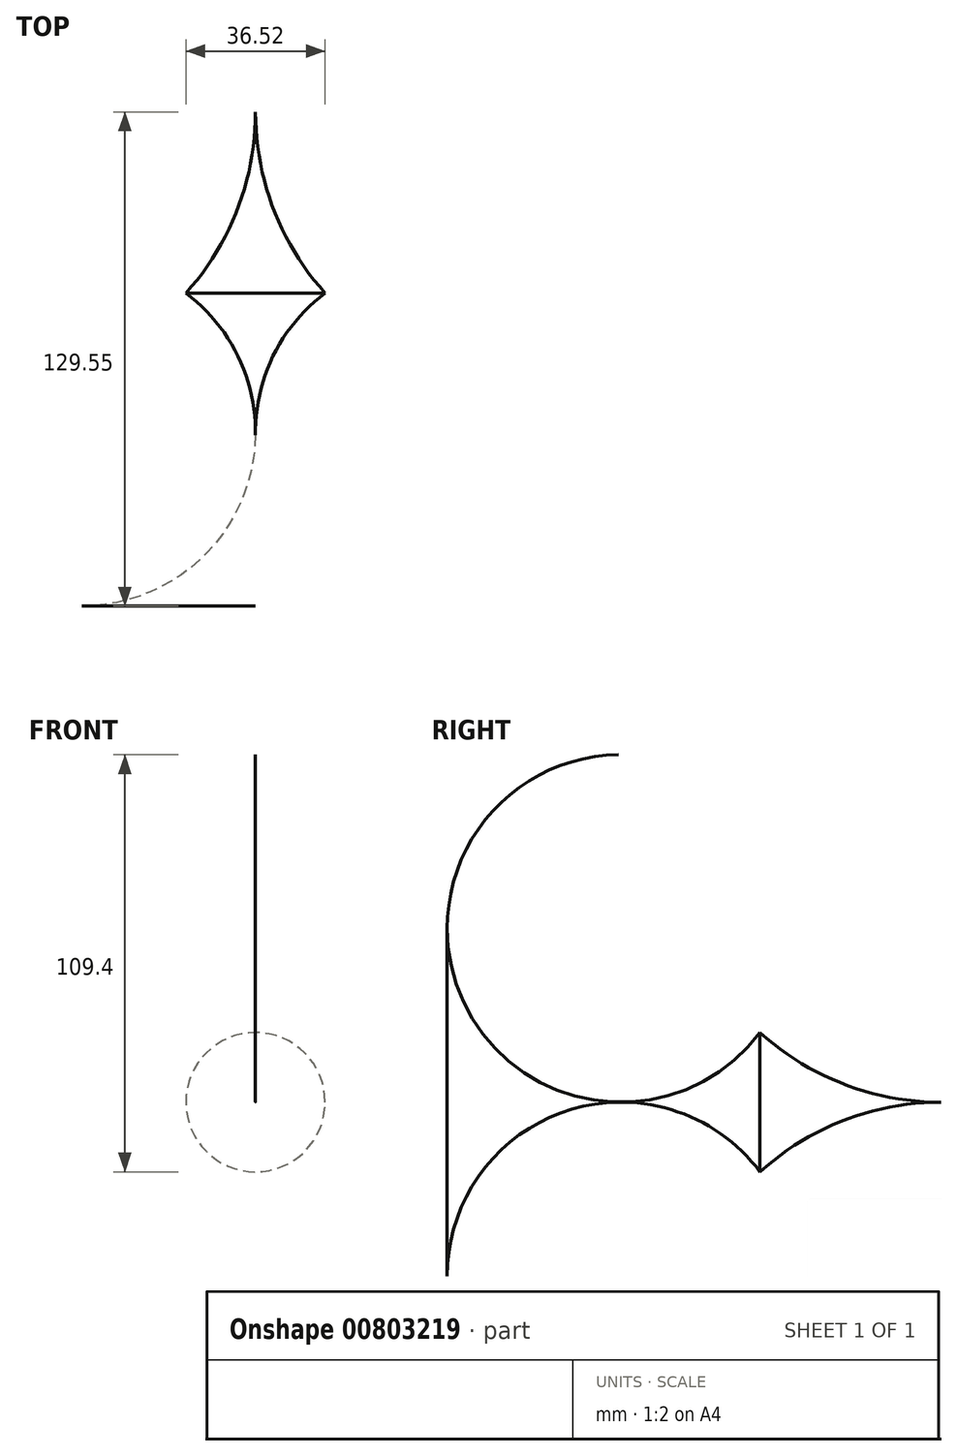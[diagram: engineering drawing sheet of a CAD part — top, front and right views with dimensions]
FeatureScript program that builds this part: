
annotation { "Feature Type Name" : "Feature", "Feature Type Description" : "" }
export const myFeature = defineFeature(function(context is Context, id is Id, definition is map)
    precondition{}
    {
        {
            var Q0;
            Q0=qCreatedBy(makeId("Top.planeOp"),FACE);
            var sketch = newSketch(context, id + "F0", { "sketchPlane" : qUnion([Q0])});
            skLineSegment(sketch, "E0", {"start": v(0, 75.28) * mm, "end": v(0, -76.95) * mm, "construction": true});
            skArc(sketch, "E1", {"start": v(18.26, 0) * mm, "mid": v(4.98, -15.77) * mm, "end": v(0, -35.79) * mm});
            skArc(sketch, "E2", {"start": v(0, 47.47) * mm, "mid": v(4.72, 22.04) * mm, "end": v(18.26, 0) * mm});
            skLineSegment(sketch, "E3", {"start": v(0, 47.47) * mm, "end": v(0, -35.79) * mm});
            skSolve(sketch);
        }
        {
            var Q0;
            Q0=makeQuery(id+"F0.imprint","IMPRINT",FACE,{"disambiguationData":[TD([[makeQuery(id+"F0.imprint","IMPRINT",EDGE,{"derivedFrom":sQuery(id+"F0.wireOp",EDGE,"E1")}),-1.0]])]});
            var Q1;
            Q1=sQuery(id+"F0.wireOp",EDGE,"E0");
            revolve(context, id + "F1", {"surfaceOperationType" : NewSurfaceOperationType.NEW, "entities" : qUnion([Q0]), "axis" : qUnion([Q1]), "revolveType" : RevolveType.FULL});
        }
    });
